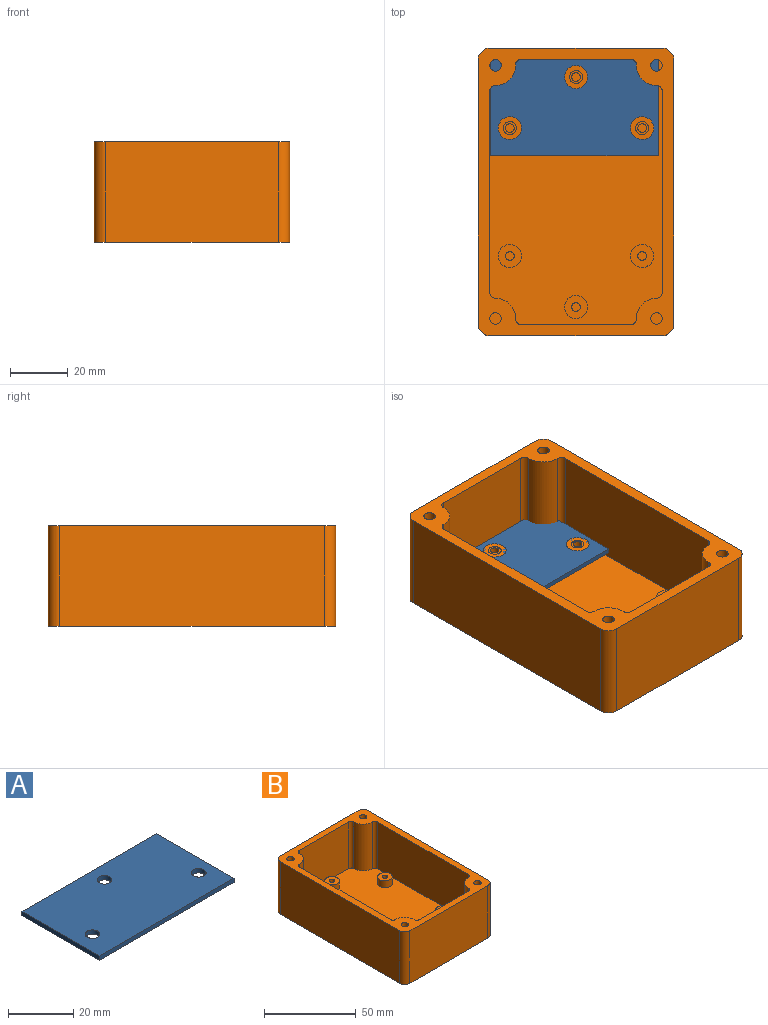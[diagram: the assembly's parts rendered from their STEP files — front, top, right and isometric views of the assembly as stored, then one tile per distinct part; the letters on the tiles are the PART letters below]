
ASSEMBLY  parts=2 mates=1
PART A: 9 faces, bbox 58.4x33.4x1.6 mm
  f0: plane 58.43x1.6mm, normal (0,1,0), area 93.5mm2, adj f1,f5,f7,f8
  f1: plane 33.42x1.6mm, normal (-1,0,0), area 53.5mm2, adj f0,f2,f7,f8
  f2: plane 58.43x1.6mm, normal (0,-1,0), area 93.5mm2, adj f1,f5,f7,f8
  f3: cylinder r=2.25mm len=4.5mm, axis (0,0,-1), area 22.6mm2, adj f7,f8
  f4: cylinder r=2.25mm len=4.5mm, axis (0,0,-1), area 22.6mm2, adj f7,f8
  f5: plane 33.42x1.6mm, normal (1,0,0), area 53.5mm2, adj f0,f2,f7,f8
  f6: cylinder r=2.25mm len=4.5mm, axis (0,0,-1), area 22.6mm2, adj f7,f8
  f7: plane 58.43x33.42mm, normal (0,0,1), area 1904.9mm2, adj f0,f1,f2,f3,f4,f5,f6
  f8: plane 58.43x33.42mm, normal (0,0,-1), area 1904.9mm2, adj f0,f1,f2,f3,f4,f5,f6
PART B: 59 faces, bbox 68x100x35 mm
  f0: plane 3x3mm, normal (0,0,1), area 7.1mm2, adj f14
  f1: plane 92.4x60mm, normal (0,0,1), area 4946.4mm2, adj f6,f7,f8,f9,f11,f15,f18,f24
  f2: plane 92x35mm, normal (-1,0,0), area 3220mm2, adj f4,f5,f12,f23
  f3: plane 60x35mm, normal (0,1,0), area 2100mm2, adj f4,f5,f12,f38
  f4: cylinder r=4mm len=35mm, axis (0,0,-1), area 219.9mm2, adj f2,f3,f5,f12
  f5: plane 100x68mm, normal (0,0,-1), area 6786.3mm2, adj f2,f3,f4,f22,f23,f37,f38,f49
  f6: plane 38x31.15mm, normal (0,-1,0), area 1183.8mm2, adj f1,f11,f12,f43
  f7: plane 70x31.15mm, normal (1,0,0), area 2180.5mm2, adj f1,f8,f12,f25
  f8: cylinder r=2mm len=31.15mm, axis (0,0,-1), area 97.9mm2, adj f1,f7,f9,f12
  f9: cylinder r=7mm len=31.15mm, axis (0,0,-1), area 347.4mm2, adj f1,f8,f11,f12
  f10: cylinder r=2mm len=31.15mm, axis (0,0,-1), area 391.4mm2, adj f12,f13
  f11: cylinder r=2mm len=31.15mm, axis (0,0,-1), area 99.2mm2, adj f1,f6,f9,f12
  f12: plane 100x68mm, normal (0,0,1), area 1488mm2, adj f2,f3,f4,f6,f7,f8,f9,f10
  f13: plane 4x4mm, normal (0,0,1), area 12.6mm2, adj f10
  f14: cylinder r=1.5mm len=4.55mm, axis (0,0,-1), area 42.9mm2, adj f0,f16
  f15: cylinder r=4mm len=8mm, axis (0,0,-1), area 114.4mm2, adj f1,f16
  f16: plane 8x8mm, normal (0,0,1), area 43.2mm2, adj f14,f15
  f17: cylinder r=1.5mm len=4.55mm, axis (0,0,-1), area 42.9mm2, adj f19,f20
  f18: cylinder r=4mm len=8mm, axis (0,0,-1), area 114.4mm2, adj f1,f19
  f19: plane 8x8mm, normal (0,0,1), area 43.2mm2, adj f17,f18
  f20: plane 3x3mm, normal (0,0,1), area 7.1mm2, adj f17
  f21: plane 3x3mm, normal (0,0,1), area 7.1mm2, adj f30
  f22: plane 60x35mm, normal (0,-1,0), area 2100mm2, adj f5,f12,f23,f49
  f23: cylinder r=4mm len=35mm, axis (0,0,-1), area 219.9mm2, adj f2,f5,f12,f22
  f24: plane 38x31.15mm, normal (0,1,0), area 1183.8mm2, adj f1,f12,f28,f53
  f25: cylinder r=2mm len=31.15mm, axis (0,0,-1), area 97.9mm2, adj f1,f7,f12,f26
  f26: cylinder r=7mm len=31.15mm, axis (0,0,-1), area 347.4mm2, adj f1,f12,f25,f28
  f27: cylinder r=2mm len=31.15mm, axis (0,0,-1), area 391.4mm2, adj f12,f29
  f28: cylinder r=2mm len=31.15mm, axis (0,0,-1), area 99.2mm2, adj f1,f12,f24,f26
  f29: plane 4x4mm, normal (0,0,1), area 12.6mm2, adj f27
  f30: cylinder r=1.5mm len=4.55mm, axis (0,0,-1), area 42.9mm2, adj f21,f32
  f31: cylinder r=4mm len=8mm, axis (0,0,-1), area 114.4mm2, adj f1,f32
  f32: plane 8x8mm, normal (0,0,1), area 43.2mm2, adj f30,f31
  f33: cylinder r=1.5mm len=4.55mm, axis (0,0,-1), area 42.9mm2, adj f35,f36
  f34: cylinder r=4mm len=8mm, axis (0,0,-1), area 114.4mm2, adj f1,f35
  f35: plane 8x8mm, normal (0,0,1), area 43.2mm2, adj f33,f34
  f36: plane 3x3mm, normal (0,0,1), area 7.1mm2, adj f33
  f37: plane 92x35mm, normal (1,0,0), area 3220mm2, adj f5,f12,f38,f49
  f38: cylinder r=4mm len=35mm, axis (0,0,-1), area 219.9mm2, adj f3,f5,f12,f37
  f39: plane 70x31.15mm, normal (-1,0,0), area 2180.5mm2, adj f1,f12,f40,f50
  f40: cylinder r=2mm len=31.15mm, axis (0,0,-1), area 97.9mm2, adj f1,f12,f39,f41
  f41: cylinder r=7mm len=31.15mm, axis (0,0,-1), area 347.4mm2, adj f1,f12,f40,f43
  f42: cylinder r=2mm len=31.15mm, axis (0,0,-1), area 391.4mm2, adj f12,f44
  f43: cylinder r=2mm len=31.15mm, axis (0,0,-1), area 99.2mm2, adj f1,f6,f12,f41
  f44: plane 4x4mm, normal (0,0,1), area 12.6mm2, adj f42
  f45: cylinder r=1.5mm len=4.55mm, axis (0,0,-1), area 42.9mm2, adj f47,f48
  f46: cylinder r=4mm len=8mm, axis (0,0,-1), area 114.4mm2, adj f1,f47
  f47: plane 8x8mm, normal (0,0,1), area 43.2mm2, adj f45,f46
  f48: plane 3x3mm, normal (0,0,1), area 7.1mm2, adj f45
  f49: cylinder r=4mm len=35mm, axis (0,0,-1), area 219.9mm2, adj f5,f12,f22,f37
  f50: cylinder r=2mm len=31.15mm, axis (0,0,-1), area 97.9mm2, adj f1,f12,f39,f51
  f51: cylinder r=7mm len=31.15mm, axis (0,0,-1), area 347.4mm2, adj f1,f12,f50,f53
  f52: cylinder r=2mm len=31.15mm, axis (0,0,-1), area 391.4mm2, adj f12,f54
  f53: cylinder r=2mm len=31.15mm, axis (0,0,-1), area 99.2mm2, adj f1,f12,f24,f51
  f54: plane 4x4mm, normal (0,0,1), area 12.6mm2, adj f52
  f55: cylinder r=1.5mm len=4.55mm, axis (0,0,-1), area 42.9mm2, adj f57,f58
  f56: cylinder r=4mm len=8mm, axis (0,0,-1), area 114.4mm2, adj f1,f57
  f57: plane 8x8mm, normal (0,0,1), area 43.2mm2, adj f55,f56
  f58: plane 3x3mm, normal (0,0,1), area 7.1mm2, adj f55
PLACE A t=(88.83,-4.27,-14.52)mm
PLACE B t=(-2.99,-4.27,-21.32)mm
MATE fastened A.f3 <-> B.f15  axis (0,0,1) through (-2.99,35.73,-12.92)mm
